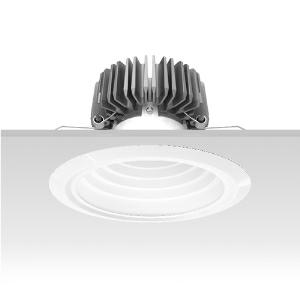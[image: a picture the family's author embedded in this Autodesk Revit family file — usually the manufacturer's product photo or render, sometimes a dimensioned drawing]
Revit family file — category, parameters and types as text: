
# Revit family: 3f_filippi_-_3f_reno_bianco_ampio_3f_filippi_-_30675_a01025_-_3f_reno_200_wh_2000-930_dali_wide___vt_wh_b617
name_source: partatom
category: Lighting Fixtures
units: mm (PartAtom-declared; Revit-internal decimal feet)

## family parameters
Cut with Voids When Loaded = No
Host = Face
Light Source = No
Part Type = Normal
Room Calculation Point = No
Round Connector Dimension = Use Diameter
Shared = No

## types (1)
- 3F Filippi - 3F Reno Bianco Ampio (1 x LED, 1804 lm, 24 W, 3000 K)
    Apparent Load = 24 VA
    Approval mark = CE
    CIE Flux Codes = 75 94 99 100 100
    Color Rendering = 90
    Color Temperature = 3000 K
    Control Gear = Electronic transformer
    Default Elevation = 1800 mm
    Description = ILLUMINOTECHNICAL
Luminous efficiency 100% (DLOR 100%, ULOR 0%).
Initial luminous flux of the luminaire 1804 lm.
Direct symmetric wide distribution.
Installation Interdistance Transv.D = 1.56 x hu - Long.D = 1.56 x hu.
Average luminance <3000 cd/m² for radial angles >65°.
Tabular UGR (CIE 117 - 4H-8H; S=0.25H; 70/50/20): RUG 20.6 - 20.5.
Beam angle: 74° - 74°.
Luminous efficacy 75 lm/W.
Lifetime (L90/B10): 30000 h. (tq+25°C)
Lifetime (L85/B10): 50000 h. (tq+25°C)
Lifetime (L70/B10): 80000 h. (tq+25°C)
Sudden decreased luminous flux after 50000 hours: 0% (C0).
Photobiological safety in compliance with IEC/TR 62778: RG0 risk exempt, (IEC 62471).
In compliance with IEC/EN 62722-2-1 - IEC/EN 62717 standards.

SOURCE
Compact LED module 2000/930.
Energy efficiency class (UE 2019/2020 - UE 2019/2015): E.
CIE 13.3 Colour rendering index: CRI >90 (R9 >50%).
IES TM-30 Fidelity Index: Rf = 92 Rg = 101.
CCT nominal colour temperature 3000 K.
Colour initial tolerance (MacAdam): SDCM 3.
Zhaga Book 3 compliant.

MECHANICAL
Passive heat dissipator in die-casting aluminium, oversized, for optimum thermal management of the LED module.
Parabolic element with graduated/concentric rings in white polycarbonate.
Transparent external lens with glossy and satin differentiated surfaces, with a cooling and anti-insect system in methacrylate (PMMA).
Fastening spring clips in stainless steel.
Dimensions: diameter 226 mm, height 146 mm. Weight 1.1 kg.
IP44 protection degree for exposed part, IP20 for recessed part.
Mechanical strength to impacts IK06 (1 joule).
Glow-wire test resistance 650°C.

ELECTRICAL
Wiring on a separate unit.
Halogen Free DALI-2 DATI (Parts 251, 252, 253), PUSH-DIM, electronic wiring 230V-50/60Hz, power factor 0.95 at full load, THD <25%, constant output current, SELV, class II, 1 driver, 1 DALI addresse.
Power of the luminaire 24 W.
ENEC - CE.
SAFE FLICKER: PstLM=<1 and SVM=<0.4 (IEC TR 61547-1 and IEC TR 63158), to ensure a more comfortable and safe light.
Luminaire compliant with EN 60598-2-22 for power supply from a centralised emergency system CPSS (Central Power Supply System), not incorporated in the luminaire - high risk areas excluded. The default power and flux are 100% in AC and 100% in DC.
Ambient temperature from 0°C to +25°C.
Temperature class T6 max 85°C.
Relative humidity UR: <85%.

INSTALLATION
Pull-up recessed fitting.
False ceiling carving: 200 mm.
All accessories dedicated to this product are available on the Catalog and on our website www.3F-Filippi.com.

ACCESSORIES
A01025 - VT transparent glass, tempered, not flammable, locked and in line with the trim, in white polycarbonate.

APPLICATIONS
Environments: architectural, commercial, exhibition areas, transit areas, corridors, shops, display windows, service areas.
In false ceilings with narrow voids.

LIGHT MANAGEMENT
Recommended minimum setting: 10%.
The luminaire, equipped with (DALI-2 DATI) driver, can be controlled manually with 3F Easy Dim technology or automatically/manually with wired or wireless DALI/D2D control systems.
The D2D driver guarantees interoperability with other devices with the same certification by making the following information available:
Device Data (Part 251), Energy Report (Part 252), Diagnosis & Maintenance (Part 253).
In electrical systems without a regulation system (manual or automatic) and DALI bus, a suitable jumper must be made on the DA-DA terminals of the appliance.

WARNING
Luminaire designed for disposal/recycling at end-of-life.
Replaceable (LED only) light source by a professional. Replaceable control gear by a professional.
    Height = 0 mm  [stored 0 ft]
    Lamp = 1 x LED
    Lamp Light Flux = 1804 lm
    Lamp Power = 24 W
    Lamp count = 1
    Length = 226 mm
    Lifetime = 50000 h
    Luminous efficacy = 75 lm/W
    Manufacturer = 3F Filippi
    ModVariant = No
    Model = 3F Filippi - 30675+A01025 - 3F Reno 200 WH 2000-930 DALI WIDE + VT WH
    Mounting Place = Ceiling
    Mounting Type = Recessed
    Number of Poles = 1
    OnlyDefault = Yes
    Power Factor = 1
    Product Name = 3F Filippi - 3F Reno Bianco Ampio
    Product group = recessed luminaire
    ProductGroupID = 4
    Protection Class = Protection class II
    Protection Degree = IP 20
    RLX_Detail_Level = 1
    RLX_Emergency_Light_Flux = 0 lm
    RLX_Emergency_Type = 0
    RLX_Emergency_Type_DB = No
    RlxData = <blob elided: 99029 chars, md5=3a81c401>
    Socket = socket
    Standby Power = 0 W
    System Light Flux = 1804 lm
    System Power = 24 W
    Type Comments = Product without accessories
    Type Image = 3ffilippi_3f_reno_200_wh__a01025.jpg
    URL = http://relux.com
    VarID = ---
    Voltage = 0 V
    Weight = 0.00 kg
    Width = 0 mm  [stored 0 ft]

note: [stored X ft] marks values corroborated as IEEE doubles in the binary element streams (Revit-internal decimal feet)

## geometry (parser evidence)
native form markers: Blend x4, Sweep x10
no freeform markers — native parametric forms only
